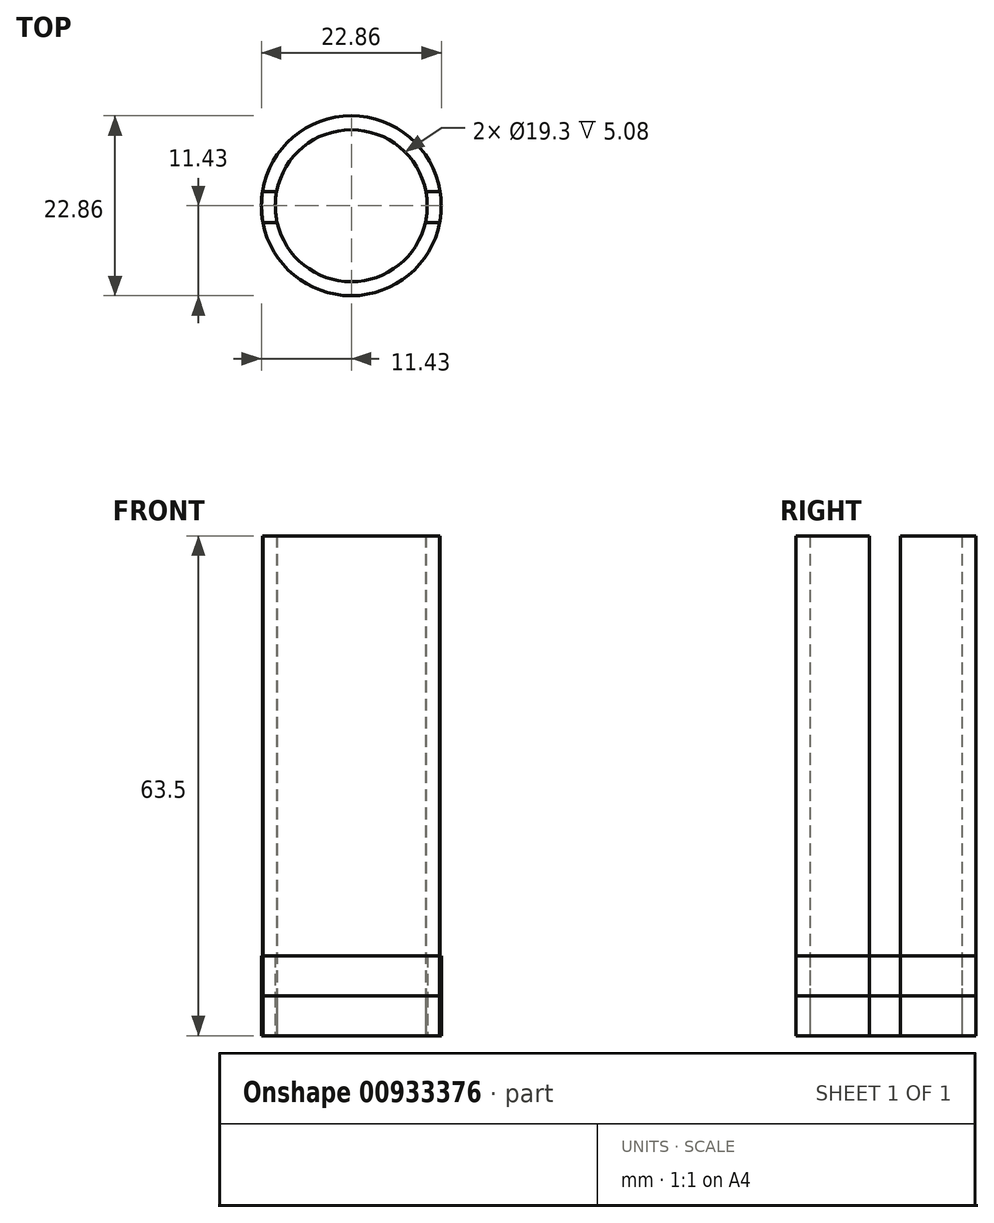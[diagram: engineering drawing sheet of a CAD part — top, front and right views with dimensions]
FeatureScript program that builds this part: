
annotation { "Feature Type Name" : "Feature", "Feature Type Description" : "" }
export const myFeature = defineFeature(function(context is Context, id is Id, definition is map)
    precondition{}
    {
        {
            var Q0;
            Q0=qCreatedBy(makeId("Top.planeOp"),FACE);
            var sketch = newSketch(context, id + "F0", { "sketchPlane" : qUnion([Q0])});
            skCircle(sketch, "E0", {"center": v(0, 0) * mm, "radius": 11.43 * mm});
            skCircle(sketch, "E1", {"center": v(0, 0) * mm, "radius": 9.65 * mm});
            skLineSegment(sketch, "E2", {"start": v(-11.29, 1.8) * mm, "end": v(11.29, 1.8) * mm});
            skLineSegment(sketch, "E3", {"start": v(-11.23, -2.13) * mm, "end": v(11.23, -2.13) * mm});
            skLineSegment(sketch, "E4", {"start": v(-11.29, 1.8) * mm, "end": v(-11.23, -2.13) * mm});
            skLineSegment(sketch, "E5", {"start": v(11.29, 1.8) * mm, "end": v(11.23, -2.13) * mm});
            skSolve(sketch);
        }
        {
            var Q0;
            {var subQ0=sQuery(id+"F0.wireOp",EDGE,"E2");var subQ4=sQuery(id+"F0.wireOp",EDGE,"E1");var subQ6=makeQuery(id+"F0.imprint","INTERSECT",VERTEX,{"disambiguationData":[OD(0.0)],"derivedFrom":[subQ4,subQ0]});Q0=makeQuery(id+"F0.imprint","IMPRINT",FACE,{"disambiguationData":[TD([[makeQuery(id+"F0.imprint","IMPRINT",EDGE,{"disambiguationData":[TD([[subQ6,1.0]])],"derivedFrom":subQ4}),-1.0]])]});}
            var Q1;
            {var subQ0=sQuery(id+"F0.wireOp",EDGE,"E3");var subQ4=sQuery(id+"F0.wireOp",EDGE,"E1");var subQ5=makeQuery(id+"F0.imprint","INTERSECT",VERTEX,{"disambiguationData":[OD(0.0)],"derivedFrom":[subQ4,subQ0]});Q1=makeQuery(id+"F0.imprint","IMPRINT",FACE,{"disambiguationData":[TD([[makeQuery(id+"F0.imprint","IMPRINT",EDGE,{"disambiguationData":[TD([[subQ5,-1.0]])],"derivedFrom":subQ4}),-1.0]])]});}
            extrude(context, id + "F1", {"entities" : qUnion([Q0, Q1]), "depth" : 63.5 * mm, "offsetDistance" : 25.4 * mm});
        }
        {
            var Q0;
            Q0 = qSketchRegion(id + "F0", true);
            extrude(context, id + "F2", {"entities" : qUnion([Q0]), "depth" : 5.08 * mm, "offsetDistance" : 25.4 * mm});
        }
        {
            var Q0;
            {var subQ0=sQuery(id+"F0.wireOp",EDGE,"E2");var subQ1=sQuery(id+"F0.wireOp",EDGE,"E1");var subQ2=makeQuery(id+"F0.imprint","INTERSECT",VERTEX,{"disambiguationData":[OD(0.0)],"derivedFrom":[subQ1,subQ0]});Q0=makeQuery(id+"F0.imprint","IMPRINT",FACE,{"disambiguationData":[TD([[makeQuery(id+"F0.imprint","IMPRINT",EDGE,{"disambiguationData":[TD([[subQ2,1.0]])],"derivedFrom":subQ1}),1.0]])]});}
            var Q1;
            {var subQ0=sQuery(id+"F0.wireOp",EDGE,"E2");var subQ1=sQuery(id+"F0.wireOp",EDGE,"E1");var subQ2=makeQuery(id+"F0.imprint","INTERSECT",VERTEX,{"disambiguationData":[OD(0.0)],"derivedFrom":[subQ1,subQ0]});Q1=makeQuery(id+"F0.imprint","IMPRINT",FACE,{"disambiguationData":[TD([[makeQuery(id+"F0.imprint","IMPRINT",EDGE,{"disambiguationData":[TD([[subQ2,-1.0]])],"derivedFrom":subQ1}),1.0]])]});}
            var Q2;
            {var subQ0=sQuery(id+"F0.wireOp",EDGE,"E3");var subQ1=sQuery(id+"F0.wireOp",EDGE,"E1");var subQ2=makeQuery(id+"F0.imprint","INTERSECT",VERTEX,{"disambiguationData":[OD(0.0)],"derivedFrom":[subQ1,subQ0]});Q2=makeQuery(id+"F0.imprint","IMPRINT",FACE,{"disambiguationData":[TD([[makeQuery(id+"F0.imprint","IMPRINT",EDGE,{"disambiguationData":[TD([[subQ2,-1.0]])],"derivedFrom":subQ1}),1.0]])]});}
            var Q3;
            {var subQ5=sQuery(id+"F0.wireOp",EDGE,"E4");Q3=makeQuery(id+"F0.imprint","IMPRINT",FACE,{"disambiguationData":[TD([[makeQuery(id+"F0.imprint","IMPRINT",EDGE,{"derivedFrom":subQ5}),1.0]])]});}
            var Q4;
            {var subQ5=sQuery(id+"F0.wireOp",EDGE,"E5");Q4=makeQuery(id+"F0.imprint","IMPRINT",FACE,{"disambiguationData":[TD([[makeQuery(id+"F0.imprint","IMPRINT",EDGE,{"derivedFrom":subQ5}),-1.0]])]});}
            var Q5;
            Q5=makeQuery(id+"F2.opExtrude","CAP_FACE",FACE,{"disambiguationData":[OSD([sQuery(id+"F0.wireOp",EDGE,"E0"),sQuery(id+"F0.wireOp",EDGE,"E1")])],"isStart":false});
            extrude(context, id + "F3", {"entities" : qUnion([Q0, Q1, Q2, Q3, Q4, Q5]), "depth" : 5.08 * mm, "offsetDistance" : 25.4 * mm});
        }
    });
